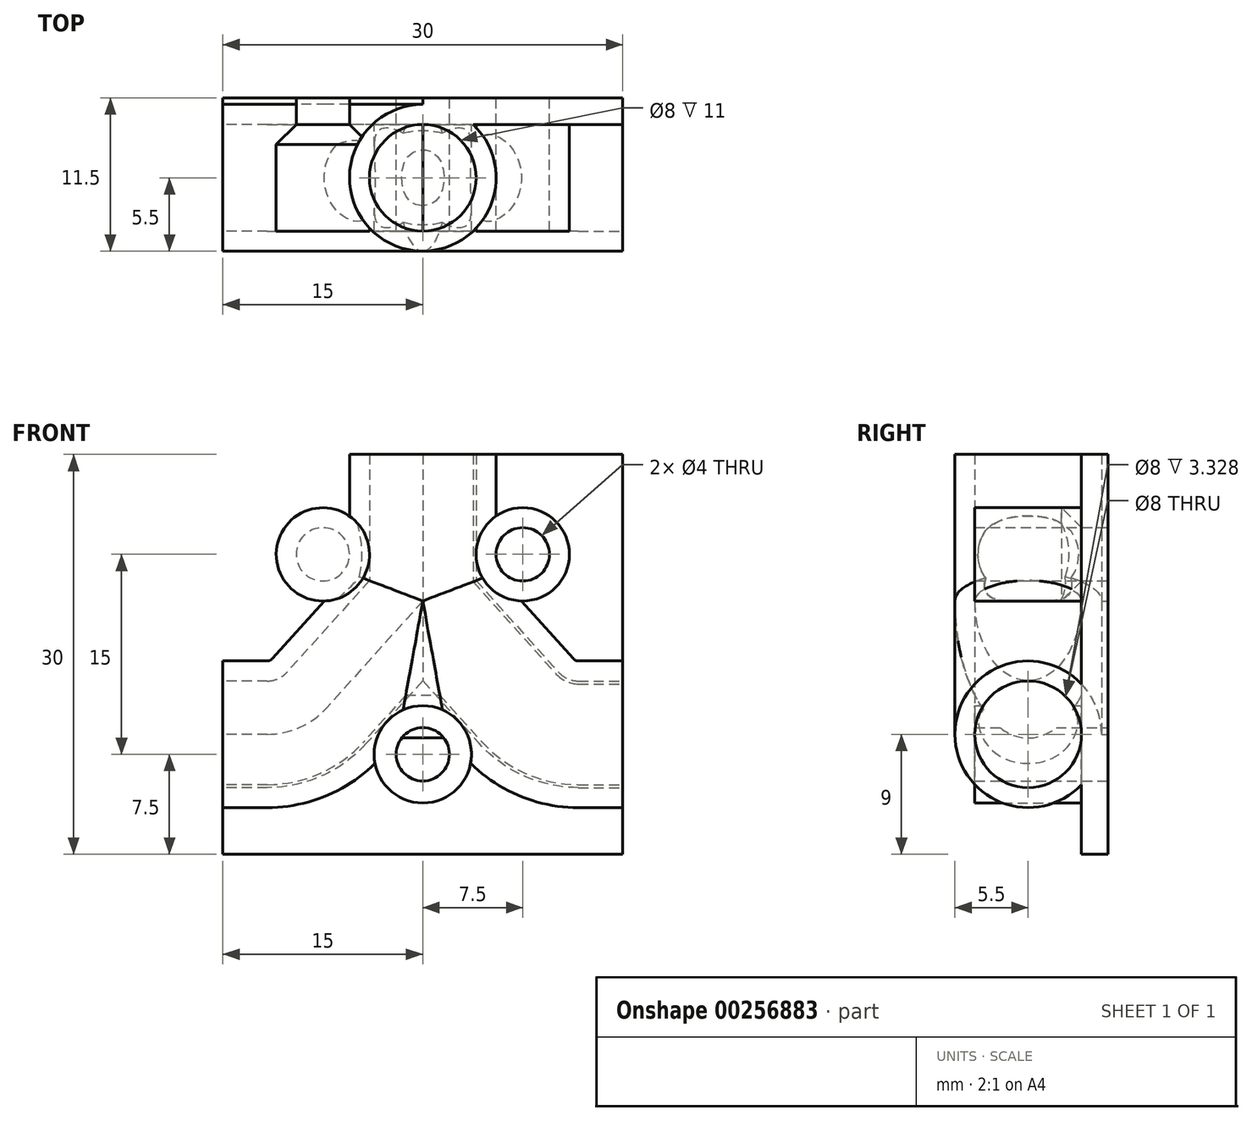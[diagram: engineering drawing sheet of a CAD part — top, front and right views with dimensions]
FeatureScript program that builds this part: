
annotation { "Feature Type Name" : "Feature", "Feature Type Description" : "" }
export const myFeature = defineFeature(function(context is Context, id is Id, definition is map)
    precondition{}
    {
        {
            var Q0;
            Q0=qCreatedBy(makeId("Front.planeOp"),FACE);
            var sketch = newSketch(context, id + "F0", { "sketchPlane" : qUnion([Q0])});
            skLineSegment(sketch, "E0.bottom", {"start": v(15, -15) * mm, "end": v(-15, -15) * mm});
            skLineSegment(sketch, "E0.top", {"start": v(15, 15) * mm, "end": v(-15, 15) * mm});
            skLineSegment(sketch, "E0.left", {"start": v(15, -15) * mm, "end": v(15, 15) * mm});
            skLineSegment(sketch, "E0.right", {"start": v(-15, -15) * mm, "end": v(-15, 15) * mm});
            skPoint(sketch, "E0.middle", {"position": v(0, 0) * mm});
            skPoint(sketch, "E1.endSnap0", {"position": v(15, 0) * mm});
            skCircle(sketch, "E2", {"center": v(7.5, 7.5) * mm, "radius": 2 * mm});
            skCircle(sketch, "E3.MirrorC", {"center": v(-7.5, 7.5) * mm, "radius": 2 * mm});
            skLineSegment(sketch, "E4", {"start": v(0, 15) * mm, "end": v(0, 4) * mm});
            skCircle(sketch, "E5", {"center": v(0, -7.5) * mm, "radius": 2 * mm});
            skLineSegment(sketch, "E6", {"start": v(0, 4) * mm, "end": v(7.21, -4.01) * mm});
            skLineSegment(sketch, "E7", {"start": v(11.67, -6) * mm, "end": v(15, -6) * mm});
            skPoint(sketch, "E8.visualSharp", {"position": v(9, -6) * mm});
            skArc(sketch, "E8.filletArc", {"start": v(7.21, -4.01) * mm, "mid": v(9.23, -5.48) * mm, "end": v(11.67, -6) * mm});
            skPoint(sketch, "E9.visualSharp", {"position": v(-9, -6) * mm});
            skLineSegment(sketch, "E10.MirrorCS", {"start": v(0, 4) * mm, "end": v(-7.21, -4.01) * mm});
            skLineSegment(sketch, "E11.MirrorCS", {"start": v(-11.67, -6) * mm, "end": v(-15, -6) * mm});
            skArc(sketch, "E12.MirrorCS", {"start": v(-7.21, -4.01) * mm, "mid": v(-9.23, -5.48) * mm, "end": v(-11.67, -6) * mm});
            skSolve(sketch);
        }
        {
            var Q0;
            Q0=makeQuery(id+"F0.imprint","IMPRINT",FACE,{"disambiguationData":[TD([[makeQuery(id+"F0.imprint","IMPRINT",EDGE,{"derivedFrom":sQuery(id+"F0.wireOp",EDGE,"E3.MirrorC")}),1.0]])]});
            var Q1;
            Q1=makeQuery(id+"F0.imprint","IMPRINT",FACE,{"disambiguationData":[TD([[makeQuery(id+"F0.imprint","IMPRINT",EDGE,{"derivedFrom":sQuery(id+"F0.wireOp",EDGE,"E2")}),-1.0]])]});
            var Q2;
            {var subQ1=sQuery(id+"F0.wireOp",EDGE,"E0.bottom");Q2=makeQuery(id+"F0.imprint","IMPRINT",FACE,{"disambiguationData":[TD([[makeQuery(id+"F0.imprint","IMPRINT",EDGE,{"derivedFrom":subQ1}),-1.0]])]});}
            extrude(context, id + "F1", {"entities" : qUnion([Q0, Q1, Q2]), "depth" : 2 * mm});
        }
        {
            var Q0;
            Q0=makeQuery(id+"F1.opExtrude","SWEPT_FACE",FACE,{"disambiguationData":[OSD([sQuery(id+"F0.wireOp",EDGE,"E0.top")])]});
            var sketch = newSketch(context, id + "F2", { "sketchPlane" : qUnion([Q0])});
            skCircle(sketch, "E13", {"center": v(0, -6) * mm, "radius": 5.5 * mm});
            skSolve(sketch);
        }
        {
            var Q0;
            {var subQ0=sQuery(id+"F2.wireOp",EDGE,"E13");var subQ1=makeQuery(id+"F1.opExtrude","CAP_EDGE",EDGE,{"disambiguationData":[OSD([sQuery(id+"F0.wireOp",EDGE,"E0.top")])],"isStart":false});var subQ2=makeQuery(id+"F2.imprint","INTERSECT",VERTEX,{"disambiguationData":[OD(0.0)],"derivedFrom":[subQ1,subQ0]});Q0=makeQuery(id+"F2.imprint","IMPRINT",FACE,{"disambiguationData":[TD([[makeQuery(id+"F2.imprint","IMPRINT",EDGE,{"disambiguationData":[TD([[subQ2,1.0]])],"derivedFrom":subQ0}),1.0]])]});}
            var Q1;
            Q1=sQuery(id+"F2.wireOp",EDGE,"SnRd2sOl-PyIU-GaBv-9RDj-R4HGwCpTsgMX");
            var Q2;
            Q2=sQuery(id+"F0.wireOp",EDGE,"E4");
            var Q3;
            Q3=sQuery(id+"F0.wireOp",EDGE,"E6");
            var Q4;
            Q4=sQuery(id+"F0.wireOp",EDGE,"E8.filletArc");
            var Q5;
            Q5=sQuery(id+"F0.wireOp",EDGE,"E7");
            sweep(context, id + "F3", {"operationType" : NewBodyOperationType.ADD, "profiles" : qUnion([Q0]), "surfaceProfiles" : qUnion([Q1]), "path" : qUnion([Q2, Q3, Q4, Q5])});
        }
        {
            var Q0;
            {var subQ0=sQuery(id+"F2.wireOp",EDGE,"E13");var subQ1=makeQuery(id+"F1.opExtrude","CAP_EDGE",EDGE,{"disambiguationData":[OSD([sQuery(id+"F0.wireOp",EDGE,"E0.top")])],"isStart":false});var subQ2=makeQuery(id+"F2.imprint","INTERSECT",VERTEX,{"disambiguationData":[OD(0.0)],"derivedFrom":[subQ1,subQ0]});Q0=makeQuery(id+"F2.imprint","IMPRINT",FACE,{"disambiguationData":[TD([[makeQuery(id+"F2.imprint","IMPRINT",EDGE,{"disambiguationData":[TD([[subQ2,1.0]])],"derivedFrom":subQ0}),1.0]])]});}
            var Q1;
            Q1=sQuery(id+"F0.wireOp",EDGE,"E4");
            var Q2;
            Q2=sQuery(id+"F0.wireOp",EDGE,"E10.MirrorCS");
            var Q3;
            Q3=sQuery(id+"F0.wireOp",EDGE,"E12.MirrorCS");
            var Q4;
            Q4=sQuery(id+"F0.wireOp",EDGE,"E11.MirrorCS");
            sweep(context, id + "F4", {"operationType" : NewBodyOperationType.ADD, "profiles" : qUnion([Q0]), "path" : qUnion([Q1, Q2, Q3, Q4])});
        }
        {
            var Q0;
            {var subQ0=sQuery(id+"F2.wireOp",EDGE,"E13");var subQ1=makeQuery(id+"F1.opExtrude","CAP_EDGE",EDGE,{"disambiguationData":[OSD([sQuery(id+"F0.wireOp",EDGE,"E0.top")])],"isStart":false});var subQ2=makeQuery(id+"F2.imprint","INTERSECT",VERTEX,{"disambiguationData":[OD(0.0)],"derivedFrom":[subQ1,subQ0]});Q0=makeQuery(id+"F2.imprint","IMPRINT",FACE,{"disambiguationData":[TD([[makeQuery(id+"F2.imprint","IMPRINT",EDGE,{"disambiguationData":[TD([[subQ2,1.0]])],"derivedFrom":subQ0}),1.0]])]});}
            var sketch = newSketch(context, id + "F5", { "sketchPlane" : qUnion([Q0])});
            skCircle(sketch, "E14", {"center": v(0, -6) * mm, "radius": 4 * mm});
            skSolve(sketch);
        }
        {
            var Q0;
            Q0=makeQuery(id+"F5.imprint","IMPRINT",FACE,{"disambiguationData":[TD([[makeQuery(id+"F5.imprint","IMPRINT",EDGE,{"derivedFrom":sQuery(id+"F5.wireOp",EDGE,"E14")}),1.0]])]});
            var Q1;
            Q1=sQuery(id+"F0.wireOp",EDGE,"E4");
            var Q2;
            Q2=sQuery(id+"F0.wireOp",EDGE,"E10.MirrorCS");
            var Q3;
            Q3=sQuery(id+"F0.wireOp",EDGE,"E12.MirrorCS");
            var Q4;
            Q4=sQuery(id+"F0.wireOp",EDGE,"E11.MirrorCS");
            sweep(context, id + "F6", {"operationType" : NewBodyOperationType.REMOVE, "profiles" : qUnion([Q0]), "path" : qUnion([Q1, Q2, Q3, Q4])});
        }
        {
            var Q0;
            Q0=makeQuery(id+"F5.imprint","IMPRINT",FACE,{"disambiguationData":[TD([[makeQuery(id+"F5.imprint","IMPRINT",EDGE,{"derivedFrom":sQuery(id+"F5.wireOp",EDGE,"E14")}),1.0]])]});
            var Q1;
            Q1=sQuery(id+"F0.wireOp",EDGE,"E4");
            var Q2;
            Q2=sQuery(id+"F0.wireOp",EDGE,"E6");
            var Q3;
            Q3=sQuery(id+"F0.wireOp",EDGE,"E8.filletArc");
            var Q4;
            Q4=sQuery(id+"F0.wireOp",EDGE,"E7");
            sweep(context, id + "F7", {"operationType" : NewBodyOperationType.REMOVE, "profiles" : qUnion([Q0]), "path" : qUnion([Q1, Q2, Q3, Q4])});
        }
        {
            var Q0;
            {var subQ1=sQuery(id+"F0.wireOp",EDGE,"E0.top");var subQ2=sQuery(id+"F0.wireOp",EDGE,"E2");var subQ3=sQuery(id+"F0.wireOp",EDGE,"E0.left");Q0=makeQuery(id+"F3.boolean.opBoolean","SPLIT",FACE,{"disambiguationData":[TD([makeQuery(id+"F1.opExtrude","SWEPT_FACE",FACE,{"disambiguationData":[OSD([subQ2])]})])],"derivedFrom":makeQuery(id+"F1.opExtrude","CAP_FACE",FACE,{"disambiguationData":[OSD([sQuery(id+"F0.wireOp",EDGE,"E0.bottom"),subQ1,subQ3,sQuery(id+"F0.wireOp",EDGE,"E0.right"),subQ2,sQuery(id+"F0.wireOp",EDGE,"E3.MirrorC"),sQuery(id+"F0.wireOp",EDGE,"E5")])],"isStart":false})});}
            var sketch = newSketch(context, id + "F8", { "sketchPlane" : qUnion([Q0])});
            skCircle(sketch, "E15", {"center": v(7.5, 7.5) * mm, "radius": 3.5 * mm});
            skSolve(sketch);
        }
        {
            var Q0;
            {var subQ1=sQuery(id+"F0.wireOp",EDGE,"E0.top");var subQ3=sQuery(id+"F0.wireOp",EDGE,"E0.right");var subQ5=sQuery(id+"F0.wireOp",EDGE,"E3.MirrorC");var subQ7=makeQuery(id+"F1.opExtrude","SWEPT_FACE",FACE,{"disambiguationData":[OSD([subQ1])]});var subQ9=sQuery(id+"F0.wireOp",EDGE,"E0.left");var subQ10=sQuery(id+"F0.wireOp",EDGE,"E5");var subQ11=sQuery(id+"F0.wireOp",EDGE,"E0.bottom");Q0=makeQuery(id+"F4.boolean.opBoolean","SPLIT",FACE,{"disambiguationData":[TD([subQ7])],"derivedFrom":makeQuery(id+"F3.boolean.opBoolean","SPLIT",FACE,{"disambiguationData":[TD([makeQuery(id+"F1.opExtrude","SWEPT_FACE",FACE,{"disambiguationData":[OSD([subQ11])]})])],"derivedFrom":makeQuery(id+"F1.opExtrude","CAP_FACE",FACE,{"disambiguationData":[OSD([subQ11,subQ1,subQ9,subQ3,sQuery(id+"F0.wireOp",EDGE,"E2"),subQ5,subQ10])],"isStart":false})})});}
            var sketch = newSketch(context, id + "F9", { "sketchPlane" : qUnion([Q0])});
            skCircle(sketch, "E16", {"center": v(-7.5, 7.5) * mm, "radius": 3.5 * mm});
            skSolve(sketch);
        }
        {
            var Q0;
            {var subQ1=sQuery(id+"F0.wireOp",EDGE,"E0.top");var subQ4=sQuery(id+"F0.wireOp",EDGE,"E0.left");var subQ7=sQuery(id+"F0.wireOp",EDGE,"E0.bottom");var subQ8=makeQuery(id+"F1.opExtrude","SWEPT_FACE",FACE,{"disambiguationData":[OSD([subQ7])]});var subQ9=sQuery(id+"F0.wireOp",EDGE,"E0.right");var subQ12=sQuery(id+"F0.wireOp",EDGE,"E5");var subQ14=sQuery(id+"F0.wireOp",EDGE,"E3.MirrorC");Q0=makeQuery(id+"F4.boolean.opBoolean","SPLIT",FACE,{"disambiguationData":[TD([subQ8])],"derivedFrom":makeQuery(id+"F3.boolean.opBoolean","SPLIT",FACE,{"disambiguationData":[TD([subQ8])],"derivedFrom":makeQuery(id+"F1.opExtrude","CAP_FACE",FACE,{"disambiguationData":[OSD([subQ7,subQ1,subQ4,subQ9,sQuery(id+"F0.wireOp",EDGE,"E2"),subQ14,subQ12])],"isStart":false})})});}
            var sketch = newSketch(context, id + "F10", { "sketchPlane" : qUnion([Q0])});
            skCircle(sketch, "E17", {"center": v(0, -7.5) * mm, "radius": 3.65 * mm});
            skSolve(sketch);
        }
        {
            var Q0;
            {var subQ0=sQuery(id+"F2.wireOp",EDGE,"E13");var subQ1=sQuery(id+"F0.wireOp",EDGE,"E0.top");var subQ2=sQuery(id+"F0.wireOp",EDGE,"E4");Q0=makeQuery(id+"F3.opSweep","SWEPT_EDGE",EDGE,{"disambiguationData":[OSD([subQ1,subQ2,subQ0]),TDD([subQ2,makeQuery(id+"F2.imprint","INTERSECT",VERTEX,{"disambiguationData":[OD(1.0)],"derivedFrom":[makeQuery(id+"F1.opExtrude","CAP_EDGE",EDGE,{"disambiguationData":[OSD([subQ1])],"isStart":false}),subQ0]})])]});}
            var Q1;
            {var subQ0=sQuery(id+"F2.wireOp",EDGE,"E13");var subQ1=sQuery(id+"F0.wireOp",EDGE,"E0.top");var subQ2=sQuery(id+"F0.wireOp",EDGE,"E10.MirrorCS");Q1=makeQuery(id+"F4.opSweep","SWEPT_EDGE",EDGE,{"disambiguationData":[OSD([subQ1,subQ2,subQ0]),TDD([subQ2,makeQuery(id+"F2.imprint","INTERSECT",VERTEX,{"disambiguationData":[OD(1.0)],"derivedFrom":[makeQuery(id+"F1.opExtrude","CAP_EDGE",EDGE,{"disambiguationData":[OSD([subQ1])],"isStart":false}),subQ0]})])]});}
            var Q2;
            {var subQ0=sQuery(id+"F2.wireOp",EDGE,"E13");var subQ1=sQuery(id+"F0.wireOp",EDGE,"E0.top");var subQ2=sQuery(id+"F0.wireOp",EDGE,"E6");Q2=makeQuery(id+"F3.opSweep","SWEPT_EDGE",EDGE,{"disambiguationData":[OSD([subQ1,subQ2,subQ0]),TDD([subQ2,makeQuery(id+"F2.imprint","INTERSECT",VERTEX,{"disambiguationData":[OD(0.0)],"derivedFrom":[makeQuery(id+"F1.opExtrude","CAP_EDGE",EDGE,{"disambiguationData":[OSD([subQ1])],"isStart":false}),subQ0]})])]});}
            var Q3;
            {var subQ0=sQuery(id+"F2.wireOp",EDGE,"E13");var subQ1=sQuery(id+"F0.wireOp",EDGE,"E0.top");var subQ2=sQuery(id+"F0.wireOp",EDGE,"E4");Q3=makeQuery(id+"F3.opSweep","SWEPT_EDGE",EDGE,{"disambiguationData":[OSD([subQ1,subQ2,subQ0]),TDD([subQ2,makeQuery(id+"F2.imprint","INTERSECT",VERTEX,{"disambiguationData":[OD(0.0)],"derivedFrom":[makeQuery(id+"F1.opExtrude","CAP_EDGE",EDGE,{"disambiguationData":[OSD([subQ1])],"isStart":false}),subQ0]})])]});}
            var Q4;
            {var subQ0=sQuery(id+"F2.wireOp",EDGE,"E13");var subQ1=sQuery(id+"F0.wireOp",EDGE,"E0.top");var subQ2=sQuery(id+"F0.wireOp",EDGE,"E8.filletArc");Q4=makeQuery(id+"F3.opSweep","SWEPT_EDGE",EDGE,{"disambiguationData":[OSD([subQ1,subQ2,subQ0]),TDD([subQ2,makeQuery(id+"F2.imprint","INTERSECT",VERTEX,{"disambiguationData":[OD(1.0)],"derivedFrom":[makeQuery(id+"F1.opExtrude","CAP_EDGE",EDGE,{"disambiguationData":[OSD([subQ1])],"isStart":false}),subQ0]})])]});}
            var Q5;
            {var subQ0=sQuery(id+"F2.wireOp",EDGE,"E13");var subQ1=sQuery(id+"F0.wireOp",EDGE,"E0.top");var subQ2=sQuery(id+"F0.wireOp",EDGE,"E10.MirrorCS");Q5=makeQuery(id+"F4.opSweep","SWEPT_EDGE",EDGE,{"disambiguationData":[OSD([subQ1,subQ2,subQ0]),TDD([subQ2,makeQuery(id+"F2.imprint","INTERSECT",VERTEX,{"disambiguationData":[OD(0.0)],"derivedFrom":[makeQuery(id+"F1.opExtrude","CAP_EDGE",EDGE,{"disambiguationData":[OSD([subQ1])],"isStart":false}),subQ0]})])]});}
            var Q6;
            {var subQ0=sQuery(id+"F2.wireOp",EDGE,"E13");Q6=makeQuery(id+"F4.boolean.opBoolean","INTERSECT",EDGE,{"derivedFrom":[makeQuery(id+"F3.opSweep","SWEPT_FACE",FACE,{"disambiguationData":[OSD([sQuery(id+"F0.wireOp",EDGE,"E6"),subQ0])]}),makeQuery(id+"F4.opSweep","SWEPT_FACE",FACE,{"disambiguationData":[OSD([sQuery(id+"F0.wireOp",EDGE,"E10.MirrorCS"),subQ0])]})]});}
            chamfer(context, id + "F11", {"entities" : qUnion([Q0, Q1, Q2, Q3, Q4, Q5, Q6]), "width" : 2.5 * mm, "tangentPropagation" : true});
        }
        {
            var Q0;
            Q0=makeQuery(id+"F9.imprint","IMPRINT",FACE,{"disambiguationData":[TD([[makeQuery(id+"F9.imprint","IMPRINT",EDGE,{"derivedFrom":sQuery(id+"F9.wireOp",EDGE,"E16")}),1.0]])]});
            var Q1;
            Q1=makeQuery(id+"F8.imprint","IMPRINT",FACE,{"disambiguationData":[TD([[makeQuery(id+"F8.imprint","IMPRINT",EDGE,{"derivedFrom":sQuery(id+"F8.wireOp",EDGE,"E15")}),1.0]])]});
            var Q2;
            Q2=makeQuery(id+"F10.imprint","IMPRINT",FACE,{"disambiguationData":[TD([[makeQuery(id+"F10.imprint","IMPRINT",EDGE,{"derivedFrom":sQuery(id+"F10.wireOp",EDGE,"E17")}),1.0]])]});
            extrude(context, id + "F12", {"entities" : qUnion([Q0, Q1, Q2]), "operationType" : NewBodyOperationType.ADD, "depth" : 8 * mm});
        }
        {
            var Q0;
            Q0=makeQuery(id+"F12.opExtrude","CAP_EDGE",EDGE,{"disambiguationData":[OSD([sQuery(id+"F8.wireOp",EDGE,"E15")])],"isStart":true});
            var Q1;
            Q1=makeQuery(id+"F12.opExtrude","CAP_EDGE",EDGE,{"disambiguationData":[OSD([sQuery(id+"F9.wireOp",EDGE,"E16")])],"isStart":true});
            var Q2;
            Q2=makeQuery(id+"F12.opExtrude","CAP_EDGE",EDGE,{"disambiguationData":[OSD([sQuery(id+"F10.wireOp",EDGE,"E17")])],"isStart":true});
            chamfer(context, id + "F13", {"entities" : qUnion([Q0, Q1, Q2]), "width" : 1.5 * mm, "tangentPropagation" : true});
        }
    });
